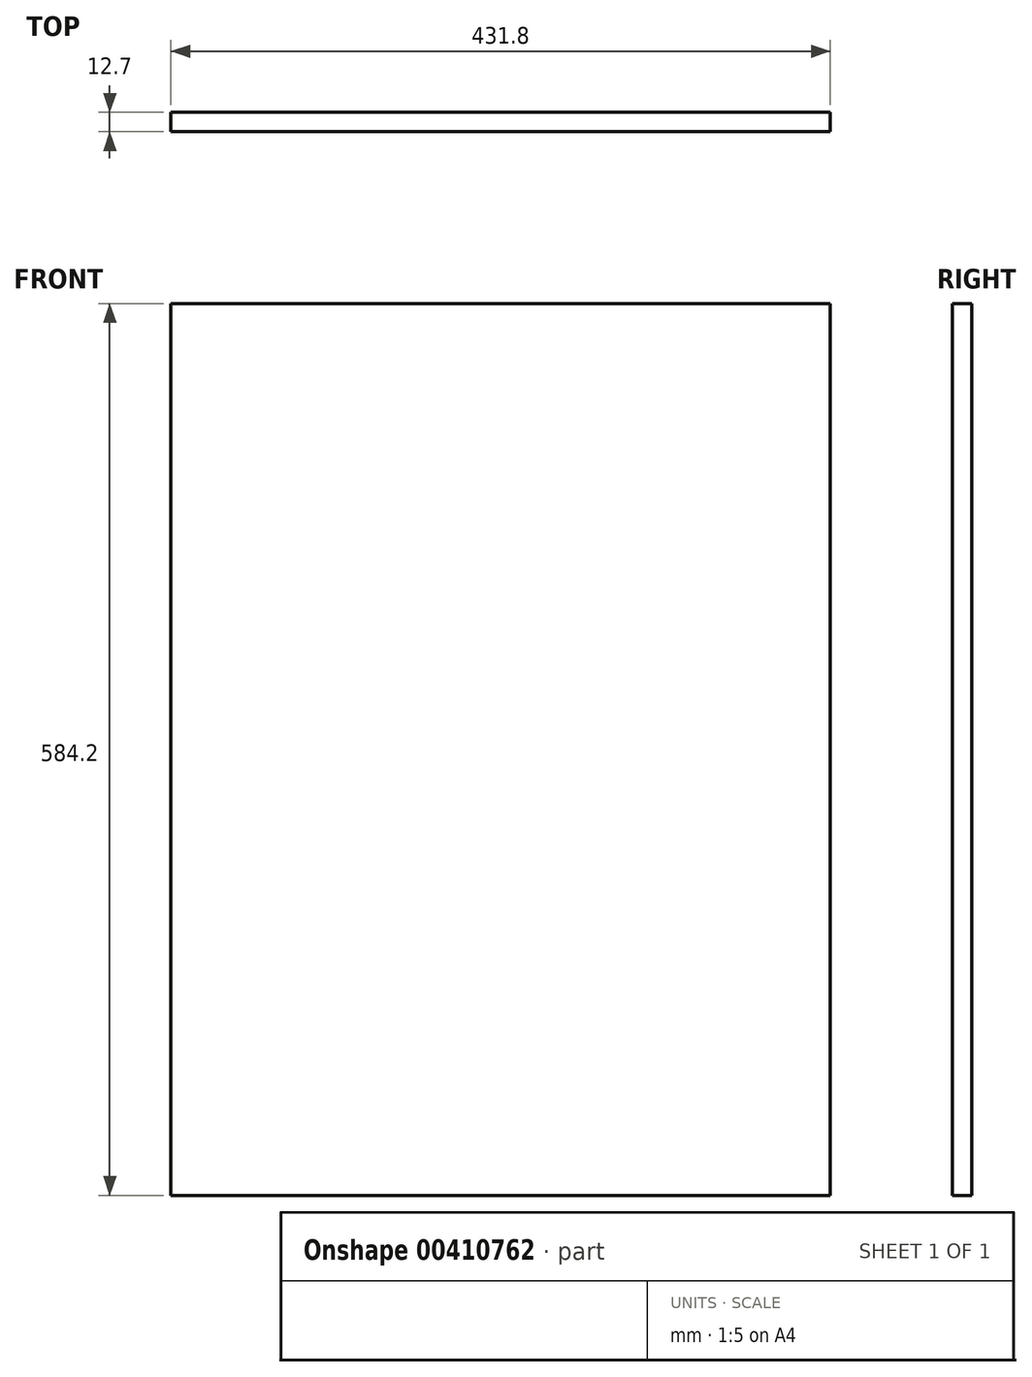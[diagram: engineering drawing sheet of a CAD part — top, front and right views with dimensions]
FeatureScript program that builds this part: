
annotation { "Feature Type Name" : "Feature", "Feature Type Description" : "" }
export const myFeature = defineFeature(function(context is Context, id is Id, definition is map)
    precondition{}
    {
        {
            var Q0;
            Q0=qCreatedBy(makeId("Front.planeOp"),FACE);
            var sketch = newSketch(context, id + "F0", { "sketchPlane" : qUnion([Q0])});
            skLineSegment(sketch, "E0.bottom", {"start": v(215.9, -304.8) * mm, "end": v(-215.9, -304.8) * mm});
            skLineSegment(sketch, "E0.top", {"start": v(215.9, 279.4) * mm, "end": v(-215.9, 279.4) * mm});
            skLineSegment(sketch, "E0.left", {"start": v(215.9, -304.8) * mm, "end": v(215.9, 279.4) * mm});
            skLineSegment(sketch, "E0.right", {"start": v(-215.9, -304.8) * mm, "end": v(-215.9, 279.4) * mm});
            skSolve(sketch);
        }
        {
            var Q0;
            Q0 = qSketchRegion(id + "F0", true);
            extrude(context, id + "F1", {"entities" : qUnion([Q0]), "depth" : 12.7 * mm});
        }
    });
